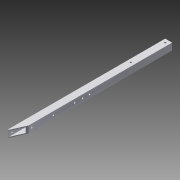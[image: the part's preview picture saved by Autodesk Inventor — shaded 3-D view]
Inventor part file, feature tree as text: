
AUTODESK INVENTOR PART (.ipt)
format: ipt  version: 2015 SP1 (Build 190203100, 203)  size: 153,600 bytes
history: native  units: in
note: dims shown in document units (in); Inventor stores cm internally (conversion verified against a paired STEP export)
features: sketch x5, hole x3, extrude x2, projected_geometry x1
ambient origin geometry x8: Origin, YZ Plane, XZ Plane, XY Plane, X Axis, Y Axis, Z Axis, Center Point
bodies: Solid1 (feature_tree)
feature tree (11):
  extrude  "Extrusion1"  Depth=1.0in
  hole  "Hole1"  [1 undecoded]
  hole  "Hole2"  [1 undecoded]
  extrude  "Extrusion4"  Depth=22.875in
  hole  "Hole3"  [1 undecoded]
  sketch  "Sketch1"  dims[d0=1.0in d1=1.0in]
  sketch  "Sketch2"  dims[d2=0.75in d3=0.75in]
  sketch  "Sketch3"  dims[d4=0.125in d5=0.125in]
  sketch  "Sketch6"  dims[d6=22.875in d7=0.0in d8=0.5in]
  projected_geometry  "Projected Loop3"
  sketch  "Sketch7"  dims[d9=0.5in d10=0.5in d11=5.5in d12=0.25in d13=0.75in d14=0.375in d15=0.25in d16=0.5635in d17=1.0in d18=0.8108in d19=0.5in d20=0.5in d21=0.5in d22=1.0in d23=8.375in d24=1.0in d25=0.5in d26=0.5in d27=0.25in d28=0.75in d29=0.375in d30=0.25in d31=0.5635in d32=1.0in d33=0.8108in d41=0.875in d42=2.0in d43=1.0in d44=0.0in d45=0.5in d46=2.5in d47=0.5in d48=0.5in d49=5.625in d50=8.75in d51=0.25in d52=0.75in d53=0.375in d54=0.25in d55=0.5635in d56=1.0in d57=0.8108in]
note: 3 required parameter values undecoded (feature->parameter linkage not recoverable at this tier; creation-order binding heuristic only, values carry confidence <= 0.55)
